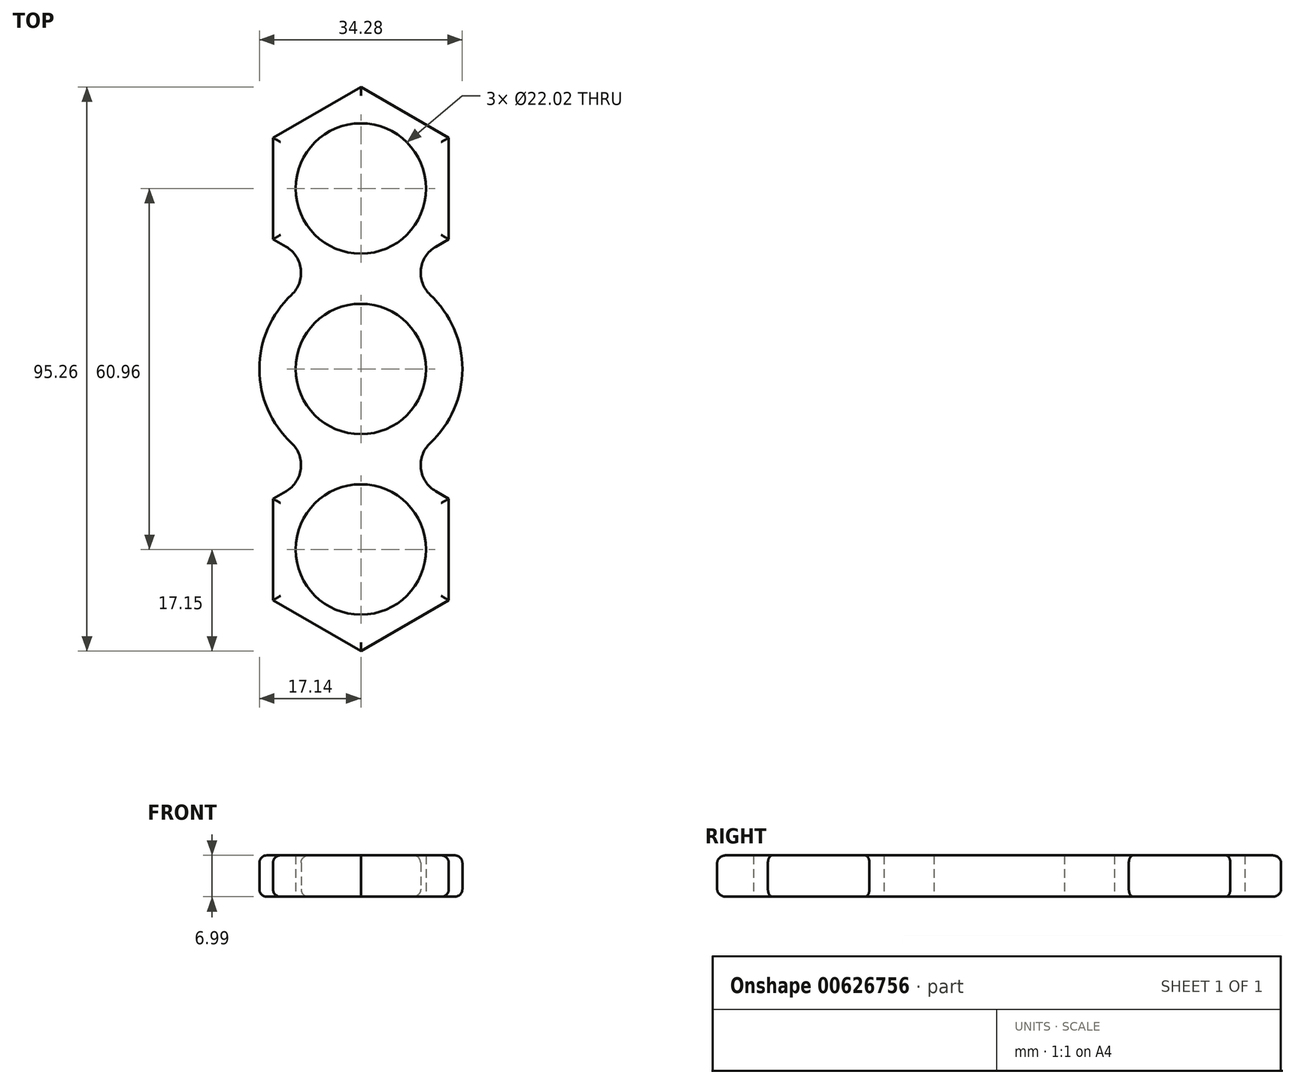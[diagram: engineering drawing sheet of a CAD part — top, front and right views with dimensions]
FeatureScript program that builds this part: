
annotation { "Feature Type Name" : "Feature", "Feature Type Description" : "" }
export const myFeature = defineFeature(function(context is Context, id is Id, definition is map)
    precondition{}
    {
        {
            var Q0;
            Q0=qCreatedBy(makeId("Top.planeOp"),FACE);
            var sketch = newSketch(context, id + "F0", { "sketchPlane" : qUnion([Q0])});
            skCircle(sketch, "E0", {"center": v(0, 0) * mm, "radius": 11.01 * mm});
            skCircle(sketch, "E1", {"center": v(0, 30.48) * mm, "radius": 11.01 * mm});
            skCircle(sketch, "E2", {"center": v(0, -30.48) * mm, "radius": 11.01 * mm});
            skLineSegment(sketch, "E3", {"start": v(0, -30.48) * mm, "end": v(0, 0) * mm});
            skLineSegment(sketch, "E4", {"start": v(0, 0) * mm, "end": v(0, 30.48) * mm});
            skCircle(sketch, "E5.cCircle", {"center": v(0, 30.48) * mm, "radius": 17.15 * mm, "construction": true});
            skLineSegment(sketch, "E5.0", {"start": v(0, 13.33) * mm, "end": v(-14.85, 21.9) * mm});
            skLineSegment(sketch, "E5.1", {"start": v(-14.85, 21.9) * mm, "end": v(-14.85, 39.05) * mm});
            skLineSegment(sketch, "E5.2", {"start": v(-14.85, 39.05) * mm, "end": v(0, 47.62) * mm});
            skLineSegment(sketch, "E5.3", {"start": v(0, 47.63) * mm, "end": v(14.85, 39.05) * mm});
            skLineSegment(sketch, "E5.4", {"start": v(14.85, 39.05) * mm, "end": v(14.85, 21.9) * mm});
            skLineSegment(sketch, "E5.5", {"start": v(14.85, 21.9) * mm, "end": v(0, 13.33) * mm});
            skCircle(sketch, "E6.cCircle", {"center": v(0, -30.48) * mm, "radius": 17.15 * mm, "construction": true});
            skLineSegment(sketch, "E6.0", {"start": v(0, -13.33) * mm, "end": v(14.85, -21.9) * mm});
            skLineSegment(sketch, "E6.1", {"start": v(14.85, -21.9) * mm, "end": v(14.85, -39.05) * mm});
            skLineSegment(sketch, "E6.2", {"start": v(14.85, -39.05) * mm, "end": v(0, -47.63) * mm});
            skLineSegment(sketch, "E6.3", {"start": v(0, -47.63) * mm, "end": v(-14.85, -39.05) * mm});
            skLineSegment(sketch, "E6.4", {"start": v(-14.85, -39.05) * mm, "end": v(-14.85, -21.9) * mm});
            skLineSegment(sketch, "E6.5", {"start": v(-14.85, -21.9) * mm, "end": v(0, -13.33) * mm});
            skCircle(sketch, "E7", {"center": v(0, 0) * mm, "radius": 17.15 * mm});
            skSolve(sketch);
        }
        {
            var Q0;
            Q0 = qSketchRegion(id + "F0", true);
            extrude(context, id + "F1", {"entities" : qUnion([Q0]), "depth" : 7 * mm, "offsetDistance" : 25.4 * mm});
        }
        {
            var Q0;
            Q0=makeQuery(id+"F1.opExtrude","SWEPT_EDGE",EDGE,{"disambiguationData":[OSD([sQuery(id+"F0.wireOp",EDGE,"E5.0"),sQuery(id+"F0.wireOp",EDGE,"E7")])]});
            var Q1;
            Q1=makeQuery(id+"F1.opExtrude","SWEPT_EDGE",EDGE,{"disambiguationData":[OSD([sQuery(id+"F0.wireOp",EDGE,"E6.5"),sQuery(id+"F0.wireOp",EDGE,"E7")])]});
            var Q2;
            Q2=makeQuery(id+"F1.opExtrude","SWEPT_EDGE",EDGE,{"disambiguationData":[OSD([sQuery(id+"F0.wireOp",EDGE,"E6.0"),sQuery(id+"F0.wireOp",EDGE,"E7")])]});
            var Q3;
            Q3=makeQuery(id+"F1.opExtrude","SWEPT_EDGE",EDGE,{"disambiguationData":[OSD([sQuery(id+"F0.wireOp",EDGE,"E5.5"),sQuery(id+"F0.wireOp",EDGE,"E7")])]});
            fillet(context, id + "F2", {"entities" : qUnion([Q0, Q1, Q2, Q3]), "radius" : 5.08 * mm, "tangentPropagation" : true, "allowEdgeOverflow" : false});
        }
        {
            var Q0;
            Q0=makeQuery(id+"F1.opExtrude","CAP_EDGE",EDGE,{"disambiguationData":[OSD([sQuery(id+"F0.wireOp",EDGE,"E5.2")])],"isStart":false});
            var Q1;
            Q1=makeQuery(id+"F1.opExtrude","CAP_EDGE",EDGE,{"disambiguationData":[OSD([sQuery(id+"F0.wireOp",EDGE,"E5.3")])],"isStart":false});
            var Q2;
            Q2=makeQuery(id+"F1.opExtrude","CAP_EDGE",EDGE,{"disambiguationData":[OSD([sQuery(id+"F0.wireOp",EDGE,"E5.4")])],"isStart":false});
            var Q3;
            Q3=makeQuery(id+"F1.opExtrude","CAP_EDGE",EDGE,{"disambiguationData":[OSD([sQuery(id+"F0.wireOp",EDGE,"E5.1")])],"isStart":false});
            var Q4;
            {var subQ0=sQuery(id+"F0.wireOp",EDGE,"E7");Q4=makeQuery(id+"F1.opExtrude","CAP_EDGE",EDGE,{"disambiguationData":[OSD([subQ0]),TDD([makeQuery(id+"F0.imprint","IMPRINT",EDGE,{"disambiguationData":[TD([[makeQuery(id+"F0.imprint","INTERSECT",VERTEX,{"derivedFrom":[sQuery(id+"F0.wireOp",EDGE,"E5.0"),subQ0]}),-1.0]])],"derivedFrom":subQ0})])],"isStart":false});}
            var Q5;
            {var subQ0=sQuery(id+"F0.wireOp",EDGE,"E7");Q5=makeQuery(id+"F1.opExtrude","CAP_EDGE",EDGE,{"disambiguationData":[OSD([subQ0]),TDD([makeQuery(id+"F0.imprint","IMPRINT",EDGE,{"disambiguationData":[TD([[makeQuery(id+"F0.imprint","INTERSECT",VERTEX,{"derivedFrom":[sQuery(id+"F0.wireOp",EDGE,"E5.5"),subQ0]}),1.0]])],"derivedFrom":subQ0})])],"isStart":false});}
            var Q6;
            Q6=makeQuery(id+"F1.opExtrude","CAP_EDGE",EDGE,{"disambiguationData":[OSD([sQuery(id+"F0.wireOp",EDGE,"E6.1")])],"isStart":false});
            var Q7;
            Q7=makeQuery(id+"F1.opExtrude","CAP_EDGE",EDGE,{"disambiguationData":[OSD([sQuery(id+"F0.wireOp",EDGE,"E6.2")])],"isStart":false});
            var Q8;
            Q8=makeQuery(id+"F1.opExtrude","CAP_EDGE",EDGE,{"disambiguationData":[OSD([sQuery(id+"F0.wireOp",EDGE,"E6.3")])],"isStart":false});
            var Q9;
            Q9=makeQuery(id+"F1.opExtrude","CAP_EDGE",EDGE,{"disambiguationData":[OSD([sQuery(id+"F0.wireOp",EDGE,"E6.4")])],"isStart":false});
            fillet(context, id + "F3", {"entities" : qUnion([Q0, Q1, Q2, Q3, Q4, Q5, Q6, Q7, Q8, Q9]), "radius" : 1.27 * mm, "tangentPropagation" : true, "allowEdgeOverflow" : false});
        }
        {
            var Q0;
            Q0=makeQuery(id+"F1.opExtrude","CAP_EDGE",EDGE,{"disambiguationData":[OSD([sQuery(id+"F0.wireOp",EDGE,"E5.3")])],"isStart":true});
            var Q1;
            Q1=makeQuery(id+"F1.opExtrude","CAP_EDGE",EDGE,{"disambiguationData":[OSD([sQuery(id+"F0.wireOp",EDGE,"E5.2")])],"isStart":true});
            var Q2;
            Q2=makeQuery(id+"F1.opExtrude","CAP_EDGE",EDGE,{"disambiguationData":[OSD([sQuery(id+"F0.wireOp",EDGE,"E5.1")])],"isStart":true});
            var Q3;
            {var subQ0=sQuery(id+"F0.wireOp",EDGE,"E7");Q3=makeQuery(id+"F1.opExtrude","CAP_EDGE",EDGE,{"disambiguationData":[OSD([subQ0]),TDD([makeQuery(id+"F0.imprint","IMPRINT",EDGE,{"disambiguationData":[TD([[makeQuery(id+"F0.imprint","INTERSECT",VERTEX,{"derivedFrom":[sQuery(id+"F0.wireOp",EDGE,"E5.0"),subQ0]}),-1.0]])],"derivedFrom":subQ0})])],"isStart":true});}
            var Q4;
            {var subQ0=sQuery(id+"F0.wireOp",EDGE,"E7");Q4=makeQuery(id+"F1.opExtrude","CAP_EDGE",EDGE,{"disambiguationData":[OSD([subQ0]),TDD([makeQuery(id+"F0.imprint","IMPRINT",EDGE,{"disambiguationData":[TD([[makeQuery(id+"F0.imprint","INTERSECT",VERTEX,{"derivedFrom":[sQuery(id+"F0.wireOp",EDGE,"E5.5"),subQ0]}),1.0]])],"derivedFrom":subQ0})])],"isStart":true});}
            var Q5;
            Q5=makeQuery(id+"F1.opExtrude","CAP_EDGE",EDGE,{"disambiguationData":[OSD([sQuery(id+"F0.wireOp",EDGE,"E5.4")])],"isStart":true});
            var Q6;
            Q6=makeQuery(id+"F1.opExtrude","CAP_EDGE",EDGE,{"disambiguationData":[OSD([sQuery(id+"F0.wireOp",EDGE,"E6.1")])],"isStart":true});
            var Q7;
            Q7=makeQuery(id+"F1.opExtrude","CAP_EDGE",EDGE,{"disambiguationData":[OSD([sQuery(id+"F0.wireOp",EDGE,"E6.2")])],"isStart":true});
            var Q8;
            Q8=makeQuery(id+"F1.opExtrude","CAP_EDGE",EDGE,{"disambiguationData":[OSD([sQuery(id+"F0.wireOp",EDGE,"E6.3")])],"isStart":true});
            var Q9;
            Q9=makeQuery(id+"F1.opExtrude","CAP_EDGE",EDGE,{"disambiguationData":[OSD([sQuery(id+"F0.wireOp",EDGE,"E6.4")])],"isStart":true});
            fillet(context, id + "F4", {"entities" : qUnion([Q0, Q1, Q2, Q3, Q4, Q5, Q6, Q7, Q8, Q9]), "radius" : 1.27 * mm, "tangentPropagation" : true, "allowEdgeOverflow" : false});
        }
    });
